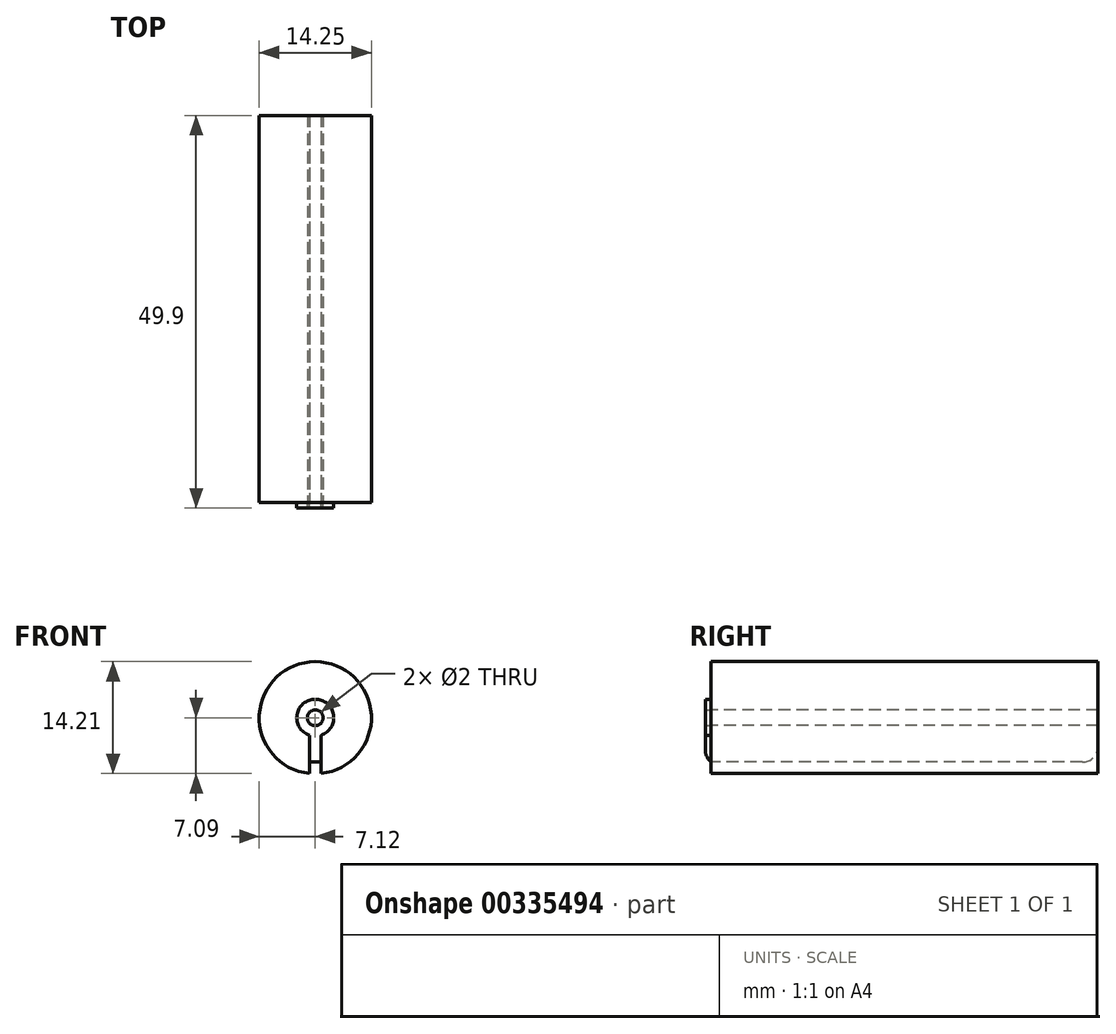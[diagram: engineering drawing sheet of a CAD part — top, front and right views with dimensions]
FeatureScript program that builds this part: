
annotation { "Feature Type Name" : "Feature", "Feature Type Description" : "" }
export const myFeature = defineFeature(function(context is Context, id is Id, definition is map)
    precondition{}
    {
        {
            var Q0;
            Q0=qCreatedBy(makeId("Front.planeOp"),FACE);
            var sketch = newSketch(context, id + "F0", { "sketchPlane" : qUnion([Q0])});
            skCircle(sketch, "E0", {"center": v(0, 0) * mm, "radius": 7.12 * mm});
            skCircle(sketch, "E1", {"center": v(0, 0) * mm, "radius": 2.35 * mm});
            skLineSegment(sketch, "E2.right", {"start": v(-0.75, 0) * mm, "end": v(-0.75, -7.09) * mm});
            skLineSegment(sketch, "E3.MirrorCS", {"start": v(0.75, 0) * mm, "end": v(0.75, -7.09) * mm});
            skLineSegment(sketch, "E4", {"start": v(-0.75, 0) * mm, "end": v(0.75, 0) * mm});
            skCircle(sketch, "E5", {"center": v(0, 0) * mm, "radius": 1 * mm});
            skLineSegment(sketch, "E6", {"start": v(-0.75, -5.64) * mm, "end": v(0.75, -5.64) * mm});
            skSolve(sketch);
        }
        {
            var Q0;
            {var subQ0=sQuery(id+"F0.wireOp",EDGE,"E2.right");var subQ1=sQuery(id+"F0.wireOp",EDGE,"E0");var subQ2=makeQuery(id+"F0.imprint","INTERSECT",VERTEX,{"derivedFrom":[subQ1,subQ0]});Q0=makeQuery(id+"F0.imprint","IMPRINT",FACE,{"disambiguationData":[TD([[makeQuery(id+"F0.imprint","IMPRINT",EDGE,{"disambiguationData":[TD([[subQ2,1.0]])],"derivedFrom":subQ1}),1.0]])]});}
            var Q1;
            {var subQ5=sQuery(id+"F0.wireOp",EDGE,"E6");Q1=makeQuery(id+"F0.imprint","IMPRINT",FACE,{"disambiguationData":[TD([[makeQuery(id+"F0.imprint","IMPRINT",EDGE,{"derivedFrom":subQ5}),1.0]])]});}
            var Q2;
            {var subQ1=sQuery(id+"F0.wireOp",EDGE,"E2.right");var subQ7=sQuery(id+"F0.wireOp",EDGE,"E1");var subQ9=makeQuery(id+"F0.imprint","INTERSECT",VERTEX,{"derivedFrom":[subQ7,subQ1]});Q2=makeQuery(id+"F0.imprint","IMPRINT",FACE,{"disambiguationData":[TD([[makeQuery(id+"F0.imprint","IMPRINT",EDGE,{"disambiguationData":[TD([[subQ9,1.0]])],"derivedFrom":subQ7}),1.0]])]});}
            var Q3;
            {var subQ1=sQuery(id+"F0.wireOp",EDGE,"E2.right");var subQ5=sQuery(id+"F0.wireOp",EDGE,"E1");var subQ6=makeQuery(id+"F0.imprint","INTERSECT",VERTEX,{"derivedFrom":[subQ5,subQ1]});Q3=makeQuery(id+"F0.imprint","IMPRINT",FACE,{"disambiguationData":[TD([[makeQuery(id+"F0.imprint","IMPRINT",EDGE,{"disambiguationData":[TD([[subQ6,-1.0]])],"derivedFrom":subQ5}),1.0]])]});}
            extrude(context, id + "F1", {"entities" : qUnion([Q0, Q1, Q2, Q3]), "oppositeDirection" : true, "depth" : 49.15 * mm});
        }
        {
            var Q0;
            {var subQ1=sQuery(id+"F0.wireOp",EDGE,"E2.right");var subQ7=sQuery(id+"F0.wireOp",EDGE,"E1");var subQ9=makeQuery(id+"F0.imprint","INTERSECT",VERTEX,{"derivedFrom":[subQ7,subQ1]});Q0=makeQuery(id+"F0.imprint","IMPRINT",FACE,{"disambiguationData":[TD([[makeQuery(id+"F0.imprint","IMPRINT",EDGE,{"disambiguationData":[TD([[subQ9,1.0]])],"derivedFrom":subQ7}),1.0]])]});}
            var Q1;
            {var subQ1=sQuery(id+"F0.wireOp",EDGE,"E2.right");var subQ5=sQuery(id+"F0.wireOp",EDGE,"E1");var subQ6=makeQuery(id+"F0.imprint","INTERSECT",VERTEX,{"derivedFrom":[subQ5,subQ1]});Q1=makeQuery(id+"F0.imprint","IMPRINT",FACE,{"disambiguationData":[TD([[makeQuery(id+"F0.imprint","IMPRINT",EDGE,{"disambiguationData":[TD([[subQ6,-1.0]])],"derivedFrom":subQ5}),1.0]])]});}
            var Q2;
            {var subQ5=sQuery(id+"F0.wireOp",EDGE,"E6");Q2=makeQuery(id+"F0.imprint","IMPRINT",FACE,{"disambiguationData":[TD([[makeQuery(id+"F0.imprint","IMPRINT",EDGE,{"derivedFrom":subQ5}),1.0]])]});}
            var Q3;
            Q3=sQuery(id+"F0.wireOp",EDGE,"E1");
            extrude(context, id + "F2", {"entities" : qUnion([Q0, Q1, Q2]), "surfaceEntities" : qUnion([Q3]), "depth" : 0.75 * mm});
        }
        {
            var Q0;
            Q0=makeQuery(id+"F2.opExtrude","CAP_EDGE",EDGE,{"disambiguationData":[OSD([sQuery(id+"F0.wireOp",EDGE,"E6")])],"isStart":false});
            fillet(context, id + "F3", {"entities" : qUnion([Q0]), "radius" : 2 * mm, "tangentPropagation" : true, "allowEdgeOverflow" : false});
        }
        {
            var Q0;
            Q0=makeQuery(id+"F1.opExtrude","CAP_EDGE",EDGE,{"disambiguationData":[OSD([sQuery(id+"F0.wireOp",EDGE,"E6")])],"isStart":false});
            fillet(context, id + "F4", {"entities" : qUnion([Q0]), "radius" : 2 * mm, "tangentPropagation" : true, "allowEdgeOverflow" : false});
        }
    });
